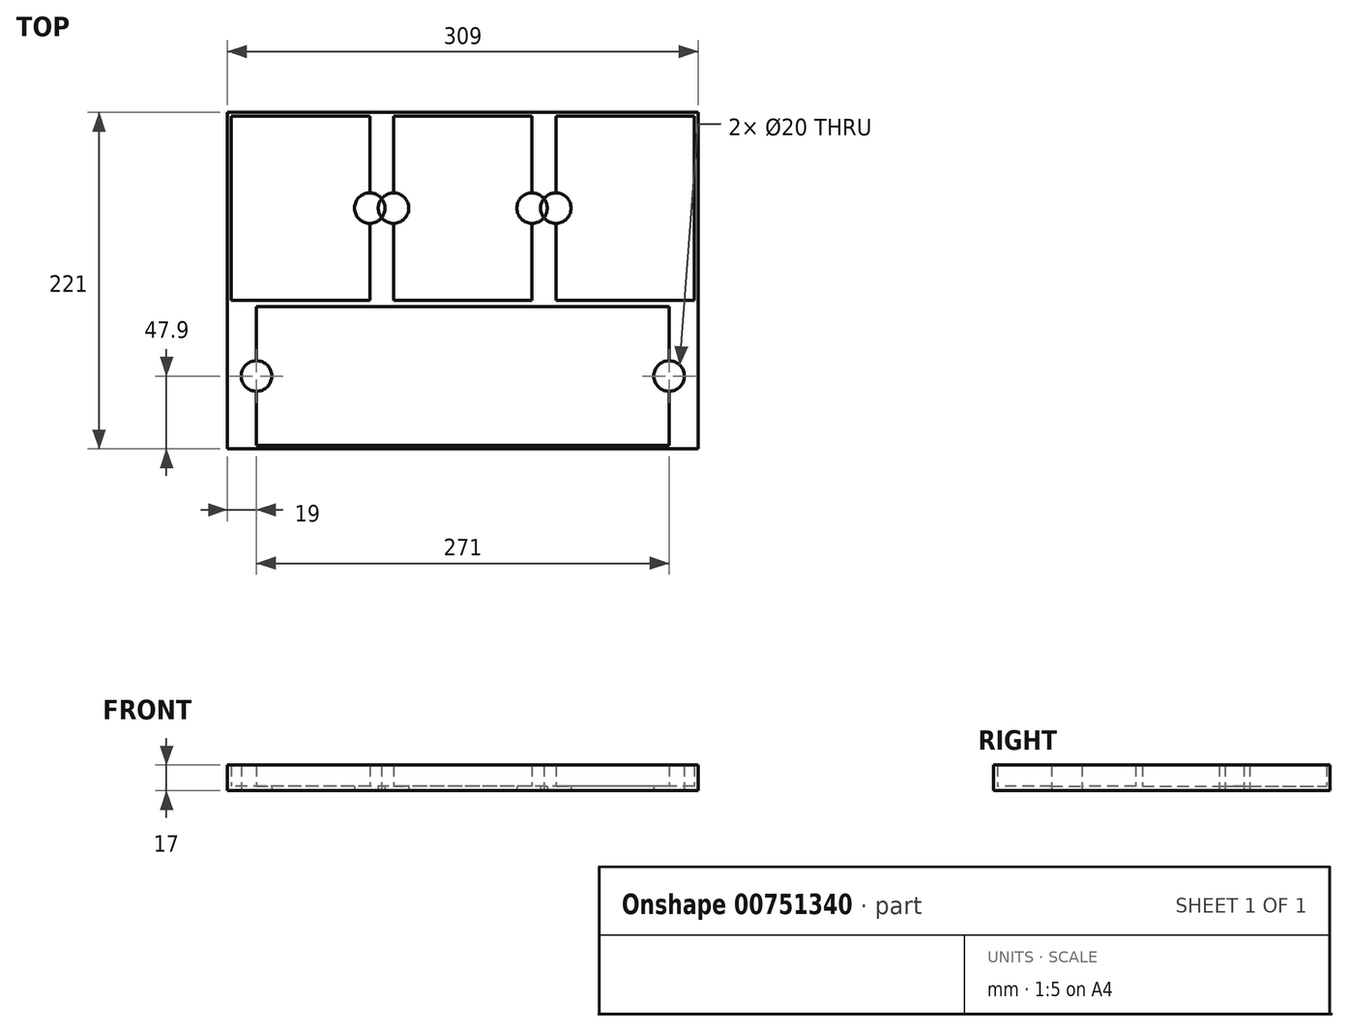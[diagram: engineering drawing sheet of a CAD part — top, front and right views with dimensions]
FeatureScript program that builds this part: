
annotation { "Feature Type Name" : "Feature", "Feature Type Description" : "" }
export const myFeature = defineFeature(function(context is Context, id is Id, definition is map)
    precondition{}
    {
        {
            var Q0;
            Q0=qCreatedBy(makeId("Top.planeOp"),FACE);
            var sketch = newSketch(context, id + "F0", { "sketchPlane" : qUnion([Q0])});
            skLineSegment(sketch, "E0.bottom", {"start": v(-154.5, 110.5) * mm, "end": v(154.5, 110.5) * mm});
            skLineSegment(sketch, "E0.top", {"start": v(-154.5, -110.5) * mm, "end": v(154.5, -110.5) * mm});
            skLineSegment(sketch, "E0.left", {"start": v(-154.5, 110.5) * mm, "end": v(-154.5, -110.5) * mm});
            skLineSegment(sketch, "E0.right", {"start": v(154.5, 110.5) * mm, "end": v(154.5, -110.5) * mm});
            skPoint(sketch, "E0.middle", {"position": v(0, 0) * mm});
            skLineSegment(sketch, "E1.bottom", {"start": v(-135.5, -108.1) * mm, "end": v(135.5, -108.1) * mm});
            skLineSegment(sketch, "E1.top", {"start": v(-135.5, -17.1) * mm, "end": v(135.5, -17.1) * mm});
            skLineSegment(sketch, "E1.left", {"start": v(-135.5, -108.1) * mm, "end": v(-135.5, -17.1) * mm});
            skLineSegment(sketch, "E1.right", {"start": v(135.5, -108.1) * mm, "end": v(135.5, -17.1) * mm});
            skPoint(sketch, "E1.middle", {"position": v(0, -50.18) * mm});
            skLineSegment(sketch, "E2.bottom", {"start": v(-45.5, 108.17) * mm, "end": v(45.5, 108.17) * mm});
            skLineSegment(sketch, "E2.top", {"start": v(-45.5, -12.83) * mm, "end": v(45.5, -12.83) * mm});
            skLineSegment(sketch, "E2.left", {"start": v(-45.5, 108.17) * mm, "end": v(-45.5, -12.83) * mm});
            skLineSegment(sketch, "E2.right", {"start": v(45.5, 108.17) * mm, "end": v(45.5, -12.83) * mm});
            skPoint(sketch, "E2.middle", {"position": v(0, 45.77) * mm});
            skLineSegment(sketch, "E3.bottom", {"start": v(61.1, 108.17) * mm, "end": v(152.1, 108.17) * mm});
            skLineSegment(sketch, "E3.top", {"start": v(61.1, -12.83) * mm, "end": v(152.1, -12.83) * mm});
            skLineSegment(sketch, "E3.left", {"start": v(61.1, 108.17) * mm, "end": v(61.1, -12.83) * mm});
            skLineSegment(sketch, "E3.right", {"start": v(152.1, 108.17) * mm, "end": v(152.1, -12.83) * mm});
            skLineSegment(sketch, "E4.bottom", {"start": v(-152.1, 108.17) * mm, "end": v(-61.1, 108.17) * mm});
            skLineSegment(sketch, "E4.top", {"start": v(-152.1, -12.83) * mm, "end": v(-61.1, -12.83) * mm});
            skLineSegment(sketch, "E4.left", {"start": v(-152.1, 108.17) * mm, "end": v(-152.1, -12.83) * mm});
            skLineSegment(sketch, "E4.right", {"start": v(-61.1, 108.17) * mm, "end": v(-61.1, -12.83) * mm});
            skCircle(sketch, "E5", {"center": v(-135.5, -62.6) * mm, "radius": 10 * mm});
            skCircle(sketch, "E6", {"center": v(135.5, -62.6) * mm, "radius": 10 * mm});
            skCircle(sketch, "E7", {"center": v(-61.1, 47.67) * mm, "radius": 10 * mm});
            skCircle(sketch, "E8", {"center": v(-45.5, 47.67) * mm, "radius": 10 * mm});
            skCircle(sketch, "E9", {"center": v(45.5, 47.67) * mm, "radius": 10 * mm});
            skCircle(sketch, "E10", {"center": v(61.1, 47.67) * mm, "radius": 10 * mm});
            skSolve(sketch);
        }
        {
            var Q0;
            {var subQ4=sQuery(id+"F0.wireOp",EDGE,"E1.bottom");Q0=makeQuery(id+"F0.imprint","IMPRINT",FACE,{"disambiguationData":[TD([[makeQuery(id+"F0.imprint","IMPRINT",EDGE,{"derivedFrom":subQ4}),1.0]])]});}
            var Q1;
            {var subQ1=sQuery(id+"F0.wireOp",EDGE,"E4.bottom");Q1=makeQuery(id+"F0.imprint","IMPRINT",FACE,{"disambiguationData":[TD([[makeQuery(id+"F0.imprint","IMPRINT",EDGE,{"derivedFrom":subQ1}),-1.0]])]});}
            var Q2;
            {var subQ0=sQuery(id+"F0.wireOp",EDGE,"E8");var subQ1=sQuery(id+"F0.wireOp",EDGE,"E7");var subQ2=makeQuery(id+"F0.imprint","INTERSECT",VERTEX,{"disambiguationData":[OD(0.0)],"derivedFrom":[subQ1,subQ0]});Q2=makeQuery(id+"F0.imprint","IMPRINT",FACE,{"disambiguationData":[TD([[makeQuery(id+"F0.imprint","IMPRINT",EDGE,{"disambiguationData":[TD([[subQ2,1.0]])],"derivedFrom":subQ1}),1.0]])]});}
            var Q3;
            {var subQ0=sQuery(id+"F0.wireOp",EDGE,"E7");var subQ1=sQuery(id+"F0.wireOp",EDGE,"E4.right");var subQ2=makeQuery(id+"F0.imprint","INTERSECT",VERTEX,{"disambiguationData":[OD(0.0)],"derivedFrom":[subQ1,subQ0]});Q3=makeQuery(id+"F0.imprint","IMPRINT",FACE,{"disambiguationData":[TD([[makeQuery(id+"F0.imprint","IMPRINT",EDGE,{"disambiguationData":[TD([[subQ2,-1.0]])],"derivedFrom":subQ1}),-1.0]])]});}
            var Q4;
            {var subQ0=sQuery(id+"F0.wireOp",EDGE,"E9");var subQ1=sQuery(id+"F0.wireOp",EDGE,"E2.right");var subQ2=makeQuery(id+"F0.imprint","INTERSECT",VERTEX,{"disambiguationData":[OD(0.0)],"derivedFrom":[subQ1,subQ0]});Q4=makeQuery(id+"F0.imprint","IMPRINT",FACE,{"disambiguationData":[TD([[makeQuery(id+"F0.imprint","IMPRINT",EDGE,{"disambiguationData":[TD([[subQ2,-1.0]])],"derivedFrom":subQ1}),-1.0]])]});}
            var Q5;
            {var subQ0=sQuery(id+"F0.wireOp",EDGE,"E10");var subQ1=sQuery(id+"F0.wireOp",EDGE,"E3.left");var subQ2=makeQuery(id+"F0.imprint","INTERSECT",VERTEX,{"disambiguationData":[OD(0.0)],"derivedFrom":[subQ1,subQ0]});Q5=makeQuery(id+"F0.imprint","IMPRINT",FACE,{"disambiguationData":[TD([[makeQuery(id+"F0.imprint","IMPRINT",EDGE,{"disambiguationData":[TD([[subQ2,-1.0]])],"derivedFrom":subQ1}),1.0]])]});}
            var Q6;
            {var subQ4=sQuery(id+"F0.wireOp",EDGE,"E3.bottom");Q6=makeQuery(id+"F0.imprint","IMPRINT",FACE,{"disambiguationData":[TD([[makeQuery(id+"F0.imprint","IMPRINT",EDGE,{"derivedFrom":subQ4}),-1.0]])]});}
            var Q7;
            {var subQ0=sQuery(id+"F0.wireOp",EDGE,"E10");var subQ1=sQuery(id+"F0.wireOp",EDGE,"E9");var subQ2=makeQuery(id+"F0.imprint","INTERSECT",VERTEX,{"disambiguationData":[OD(0.0)],"derivedFrom":[subQ1,subQ0]});Q7=makeQuery(id+"F0.imprint","IMPRINT",FACE,{"disambiguationData":[TD([[makeQuery(id+"F0.imprint","IMPRINT",EDGE,{"disambiguationData":[TD([[subQ2,1.0]])],"derivedFrom":subQ1}),1.0]])]});}
            var Q8;
            {var subQ0=sQuery(id+"F0.wireOp",EDGE,"E6");var subQ1=sQuery(id+"F0.wireOp",EDGE,"E1.right");var subQ2=makeQuery(id+"F0.imprint","INTERSECT",VERTEX,{"disambiguationData":[OD(0.0)],"derivedFrom":[subQ1,subQ0]});Q8=makeQuery(id+"F0.imprint","IMPRINT",FACE,{"disambiguationData":[TD([[makeQuery(id+"F0.imprint","IMPRINT",EDGE,{"disambiguationData":[TD([[subQ2,-1.0]])],"derivedFrom":subQ1}),-1.0]])]});}
            var Q9;
            {var subQ0=sQuery(id+"F0.wireOp",EDGE,"E8");var subQ1=sQuery(id+"F0.wireOp",EDGE,"E2.left");var subQ2=makeQuery(id+"F0.imprint","INTERSECT",VERTEX,{"disambiguationData":[OD(0.0)],"derivedFrom":[subQ1,subQ0]});Q9=makeQuery(id+"F0.imprint","IMPRINT",FACE,{"disambiguationData":[TD([[makeQuery(id+"F0.imprint","IMPRINT",EDGE,{"disambiguationData":[TD([[subQ2,-1.0]])],"derivedFrom":subQ1}),1.0]])]});}
            var Q10;
            {var subQ0=sQuery(id+"F0.wireOp",EDGE,"E8");var subQ1=sQuery(id+"F0.wireOp",EDGE,"E2.left");var subQ2=makeQuery(id+"F0.imprint","INTERSECT",VERTEX,{"disambiguationData":[OD(0.0)],"derivedFrom":[subQ1,subQ0]});Q10=makeQuery(id+"F0.imprint","IMPRINT",FACE,{"disambiguationData":[TD([[makeQuery(id+"F0.imprint","IMPRINT",EDGE,{"disambiguationData":[TD([[subQ2,-1.0]])],"derivedFrom":subQ1}),-1.0]])]});}
            var Q11;
            {var subQ0=sQuery(id+"F0.wireOp",EDGE,"E6");var subQ1=sQuery(id+"F0.wireOp",EDGE,"E1.right");var subQ2=makeQuery(id+"F0.imprint","INTERSECT",VERTEX,{"disambiguationData":[OD(0.0)],"derivedFrom":[subQ1,subQ0]});Q11=makeQuery(id+"F0.imprint","IMPRINT",FACE,{"disambiguationData":[TD([[makeQuery(id+"F0.imprint","IMPRINT",EDGE,{"disambiguationData":[TD([[subQ2,-1.0]])],"derivedFrom":subQ1}),1.0]])]});}
            var Q12;
            {var subQ0=sQuery(id+"F0.wireOp",EDGE,"E5");var subQ1=sQuery(id+"F0.wireOp",EDGE,"E1.left");var subQ2=makeQuery(id+"F0.imprint","INTERSECT",VERTEX,{"disambiguationData":[OD(0.0)],"derivedFrom":[subQ1,subQ0]});Q12=makeQuery(id+"F0.imprint","IMPRINT",FACE,{"disambiguationData":[TD([[makeQuery(id+"F0.imprint","IMPRINT",EDGE,{"disambiguationData":[TD([[subQ2,-1.0]])],"derivedFrom":subQ1}),-1.0]])]});}
            var Q13;
            {var subQ0=sQuery(id+"F0.wireOp",EDGE,"E5");var subQ1=sQuery(id+"F0.wireOp",EDGE,"E1.left");var subQ2=makeQuery(id+"F0.imprint","INTERSECT",VERTEX,{"disambiguationData":[OD(0.0)],"derivedFrom":[subQ1,subQ0]});Q13=makeQuery(id+"F0.imprint","IMPRINT",FACE,{"disambiguationData":[TD([[makeQuery(id+"F0.imprint","IMPRINT",EDGE,{"disambiguationData":[TD([[subQ2,-1.0]])],"derivedFrom":subQ1}),1.0]])]});}
            var Q14;
            {var subQ0=sQuery(id+"F0.wireOp",EDGE,"E10");var subQ1=sQuery(id+"F0.wireOp",EDGE,"E3.left");var subQ2=makeQuery(id+"F0.imprint","INTERSECT",VERTEX,{"disambiguationData":[OD(0.0)],"derivedFrom":[subQ1,subQ0]});Q14=makeQuery(id+"F0.imprint","IMPRINT",FACE,{"disambiguationData":[TD([[makeQuery(id+"F0.imprint","IMPRINT",EDGE,{"disambiguationData":[TD([[subQ2,-1.0]])],"derivedFrom":subQ1}),-1.0]])]});}
            var Q15;
            {var subQ4=sQuery(id+"F0.wireOp",EDGE,"E2.bottom");Q15=makeQuery(id+"F0.imprint","IMPRINT",FACE,{"disambiguationData":[TD([[makeQuery(id+"F0.imprint","IMPRINT",EDGE,{"derivedFrom":subQ4}),-1.0]])]});}
            var Q16;
            {var subQ0=sQuery(id+"F0.wireOp",EDGE,"E9");var subQ1=sQuery(id+"F0.wireOp",EDGE,"E2.right");var subQ2=makeQuery(id+"F0.imprint","INTERSECT",VERTEX,{"disambiguationData":[OD(0.0)],"derivedFrom":[subQ1,subQ0]});Q16=makeQuery(id+"F0.imprint","IMPRINT",FACE,{"disambiguationData":[TD([[makeQuery(id+"F0.imprint","IMPRINT",EDGE,{"disambiguationData":[TD([[subQ2,-1.0]])],"derivedFrom":subQ1}),1.0]])]});}
            var Q17;
            Q17=makeQuery(id+"F0.imprint","IMPRINT",FACE,{"disambiguationData":[TD([[makeQuery(id+"F0.imprint","IMPRINT",EDGE,{"derivedFrom":sQuery(id+"F0.wireOp",EDGE,"E0.bottom")}),-1.0]])]});
            var Q18;
            {var subQ0=sQuery(id+"F0.wireOp",EDGE,"E7");var subQ1=sQuery(id+"F0.wireOp",EDGE,"E4.right");var subQ2=makeQuery(id+"F0.imprint","INTERSECT",VERTEX,{"disambiguationData":[OD(0.0)],"derivedFrom":[subQ1,subQ0]});Q18=makeQuery(id+"F0.imprint","IMPRINT",FACE,{"disambiguationData":[TD([[makeQuery(id+"F0.imprint","IMPRINT",EDGE,{"disambiguationData":[TD([[subQ2,-1.0]])],"derivedFrom":subQ1}),1.0]])]});}
            extrude(context, id + "F1", {"entities" : qUnion([Q0, Q1, Q2, Q3, Q4, Q5, Q6, Q7, Q8, Q9, Q10, Q11, Q12, Q13, Q14, Q15, Q16, Q17, Q18]), "depth" : 3 * mm, "offsetDistance" : 25 * mm});
        }
        {
            var Q0;
            Q0=makeQuery(id+"F0.imprint","IMPRINT",FACE,{"disambiguationData":[TD([[makeQuery(id+"F0.imprint","IMPRINT",EDGE,{"derivedFrom":sQuery(id+"F0.wireOp",EDGE,"E0.bottom")}),-1.0]])]});
            extrude(context, id + "F2", {"entities" : qUnion([Q0]), "operationType" : NewBodyOperationType.ADD, "depth" : 17 * mm, "offsetDistance" : 25 * mm});
        }
    });
